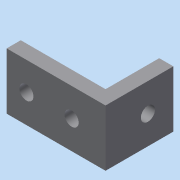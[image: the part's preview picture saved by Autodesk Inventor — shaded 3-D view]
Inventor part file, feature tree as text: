
AUTODESK INVENTOR PART (.ipt)
format: ipt  version: 2015 (Build 190159000, 159)  size: 102,912 bytes
history: native  units: mm
features: sketch x3, hole x2, extrude x1
ambient origin geometry x8: Origin, YZ Plane, XZ Plane, XY Plane, X Axis, Y Axis, Z Axis, Center Point
bodies: Solid1 (feature_tree)
feature tree (6):
  extrude  "Extrusion1"  Depth=5.0mm
  hole  "Hole1"  [1 undecoded]
  hole  "Hole2"  [1 undecoded]
  sketch  "Sketch1"  dims[d0=5.0mm d1=5.0mm]
  sketch  "Sketch2"  dims[d2=35.0mm d3=19.0mm]
  sketch  "Sketch3"  dims[d4=20.0mm d5=0.0mm d6=10.0mm d7=7.0mm d8=7.0mm d9=5.0mm d10=6.0mm d11=4.0mm d12=2.0mm d13=90.0deg d14=8.0mm d15=20.594885mm d18=10.0mm d19=10.0mm d20=5.0mm d21=6.0mm d22=4.0mm d23=2.0mm d24=90.0deg d25=8.0mm d26=20.594885mm]
note: 2 required parameter values undecoded (feature->parameter linkage not recoverable at this tier; creation-order binding heuristic only, values carry confidence <= 0.55)
